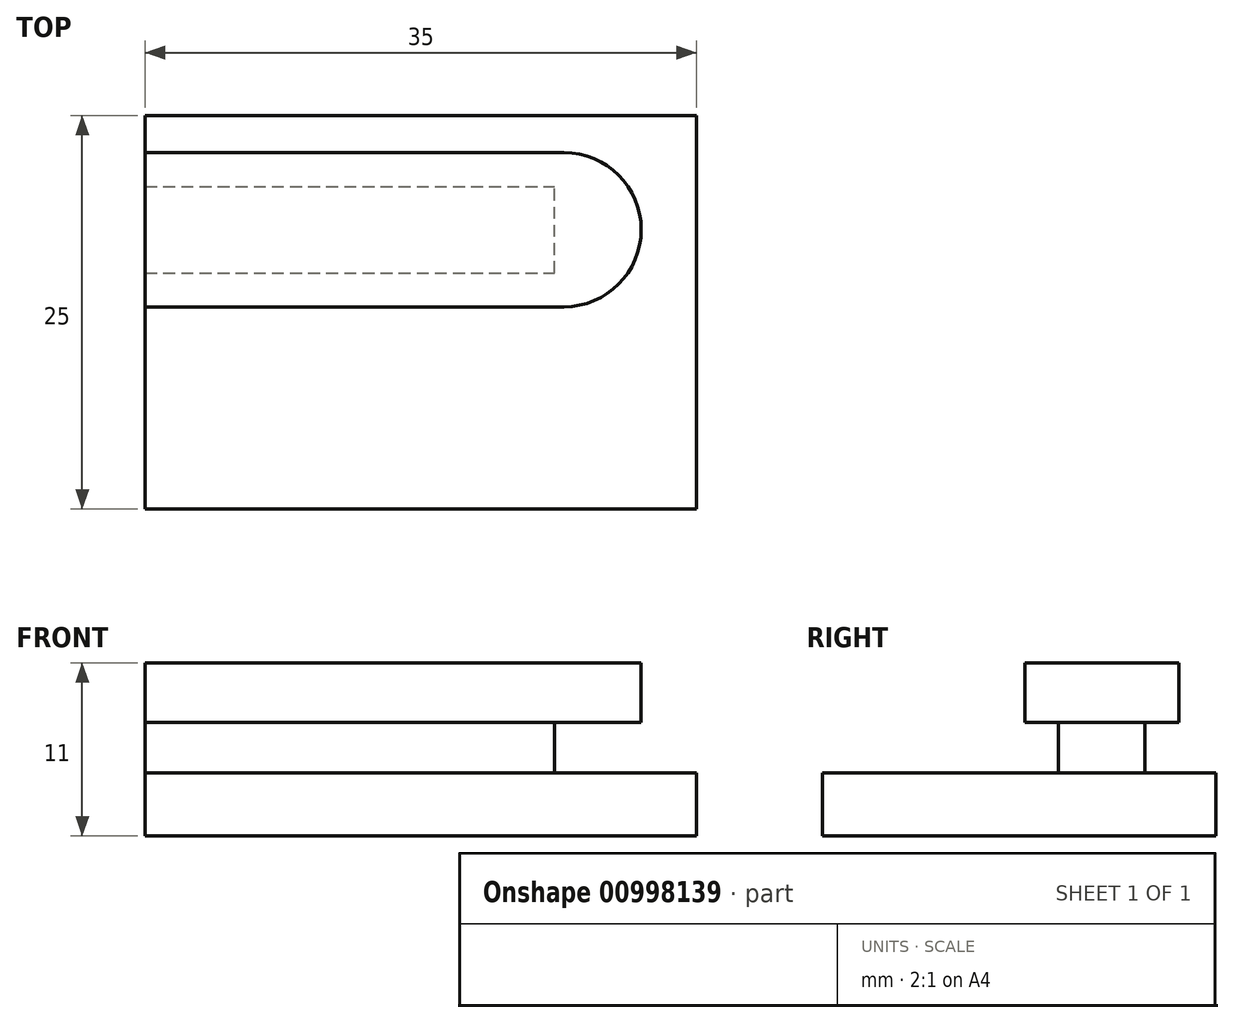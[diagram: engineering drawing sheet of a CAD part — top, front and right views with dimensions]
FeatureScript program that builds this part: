
annotation { "Feature Type Name" : "Feature", "Feature Type Description" : "" }
export const myFeature = defineFeature(function(context is Context, id is Id, definition is map)
    precondition{}
    {
        {
            var Q0;
            Q0=qCreatedBy(makeId("Top.planeOp"),FACE);
            var sketch = newSketch(context, id + "F0", { "sketchPlane" : qUnion([Q0])});
            skLineSegment(sketch, "E0.bottom", {"start": v(-35, 15.35) * mm, "end": v(0, 15.35) * mm});
            skLineSegment(sketch, "E0.top", {"start": v(-35, -9.65) * mm, "end": v(0, -9.65) * mm});
            skLineSegment(sketch, "E0.left", {"start": v(-35, 15.35) * mm, "end": v(-35, -9.65) * mm});
            skLineSegment(sketch, "E0.right", {"start": v(0, 15.35) * mm, "end": v(0, -9.65) * mm});
            skSolve(sketch);
        }
        {
            var Q0;
            Q0 = qSketchRegion(id + "F0", true);
            extrude(context, id + "F1", {"entities" : qUnion([Q0]), "depth" : 4 * mm, "offsetDistance" : 25 * mm});
        }
        {
            var Q0;
            Q0=makeQuery(id+"F1.opExtrude","CAP_FACE",FACE,{"disambiguationData":[OSD([sQuery(id+"F0.wireOp",EDGE,"E0.bottom"),sQuery(id+"F0.wireOp",EDGE,"E0.top"),sQuery(id+"F0.wireOp",EDGE,"E0.left"),sQuery(id+"F0.wireOp",EDGE,"E0.right")])],"isStart":false});
            var sketch = newSketch(context, id + "F2", { "sketchPlane" : qUnion([Q0])});
            skLineSegment(sketch, "E1.bottom", {"start": v(-35, 5.35) * mm, "end": v(-9, 5.35) * mm});
            skLineSegment(sketch, "E1.top", {"start": v(-35, 10.85) * mm, "end": v(-9, 10.85) * mm});
            skLineSegment(sketch, "E1.left", {"start": v(-35, 5.35) * mm, "end": v(-35, 10.85) * mm});
            skLineSegment(sketch, "E1.right", {"start": v(-9, 5.35) * mm, "end": v(-9, 10.85) * mm});
            skSolve(sketch);
        }
        {
            var Q0;
            Q0=makeQuery(id+"F2.imprint","IMPRINT",FACE,{"disambiguationData":[TD([[makeQuery(id+"F2.imprint","IMPRINT",EDGE,{"derivedFrom":sQuery(id+"F2.wireOp",EDGE,"E1.bottom")}),1.0]])]});
            extrude(context, id + "F3", {"entities" : qUnion([Q0]), "operationType" : NewBodyOperationType.ADD, "depth" : 3.2 * mm, "offsetDistance" : 25 * mm});
        }
        {
            var Q0;
            Q0=makeQuery(id+"F3.opExtrude","CAP_FACE",FACE,{"disambiguationData":[OSD([sQuery(id+"F2.wireOp",EDGE,"E1.bottom"),sQuery(id+"F2.wireOp",EDGE,"E1.top"),sQuery(id+"F2.wireOp",EDGE,"E1.left"),sQuery(id+"F2.wireOp",EDGE,"E1.right")])],"isStart":false});
            var sketch = newSketch(context, id + "F4", { "sketchPlane" : qUnion([Q0])});
            skLineSegment(sketch, "E2.bottom", {"start": v(-35, 3.2) * mm, "end": v(-8.4, 3.2) * mm});
            skLineSegment(sketch, "E2.top", {"start": v(-35, 13) * mm, "end": v(-8.4, 13) * mm});
            skLineSegment(sketch, "E2.left", {"start": v(-35, 3.2) * mm, "end": v(-35, 13) * mm});
            skLineSegment(sketch, "E2.right", {"start": v(-3.5, 8.1) * mm, "end": v(-3.5, 8.1) * mm});
            skLineSegment(sketch, "E3", {"start": v(-35, 8.1) * mm, "end": v(-3.5, 8.1) * mm, "construction": true});
            skPoint(sketch, "E4.visualSharp", {"position": v(-3.5, 3.2) * mm});
            skArc(sketch, "E4.filletArc", {"start": v(-8.4, 3.2) * mm, "mid": v(-4.94, 4.64) * mm, "end": v(-3.5, 8.1) * mm});
            skPoint(sketch, "E5.visualSharp", {"position": v(-3.5, 13) * mm});
            skArc(sketch, "E5.filletArc", {"start": v(-3.5, 8.1) * mm, "mid": v(-4.94, 11.57) * mm, "end": v(-8.4, 13) * mm});
            skSolve(sketch);
        }
        {
            var Q0;
            {var subQ4=sQuery(id+"F4.wireOp",EDGE,"E2.bottom");Q0=makeQuery(id+"F4.imprint","IMPRINT",FACE,{"disambiguationData":[TD([[makeQuery(id+"F4.imprint","IMPRINT",EDGE,{"derivedFrom":subQ4}),1.0]])]});}
            var Q1;
            {var subQ1=makeQuery(id+"F3.opExtrude","CAP_EDGE",EDGE,{"disambiguationData":[OSD([sQuery(id+"F2.wireOp",EDGE,"E1.bottom")])],"isStart":false});Q1=makeQuery(id+"F4.imprint","IMPRINT",FACE,{"disambiguationData":[TD([[makeQuery(id+"F4.imprint","IMPRINT",EDGE,{"derivedFrom":subQ1}),1.0]])]});}
            extrude(context, id + "F5", {"entities" : qUnion([Q0, Q1]), "operationType" : NewBodyOperationType.ADD, "depth" : 3.8 * mm, "offsetDistance" : 25 * mm});
        }
    });
